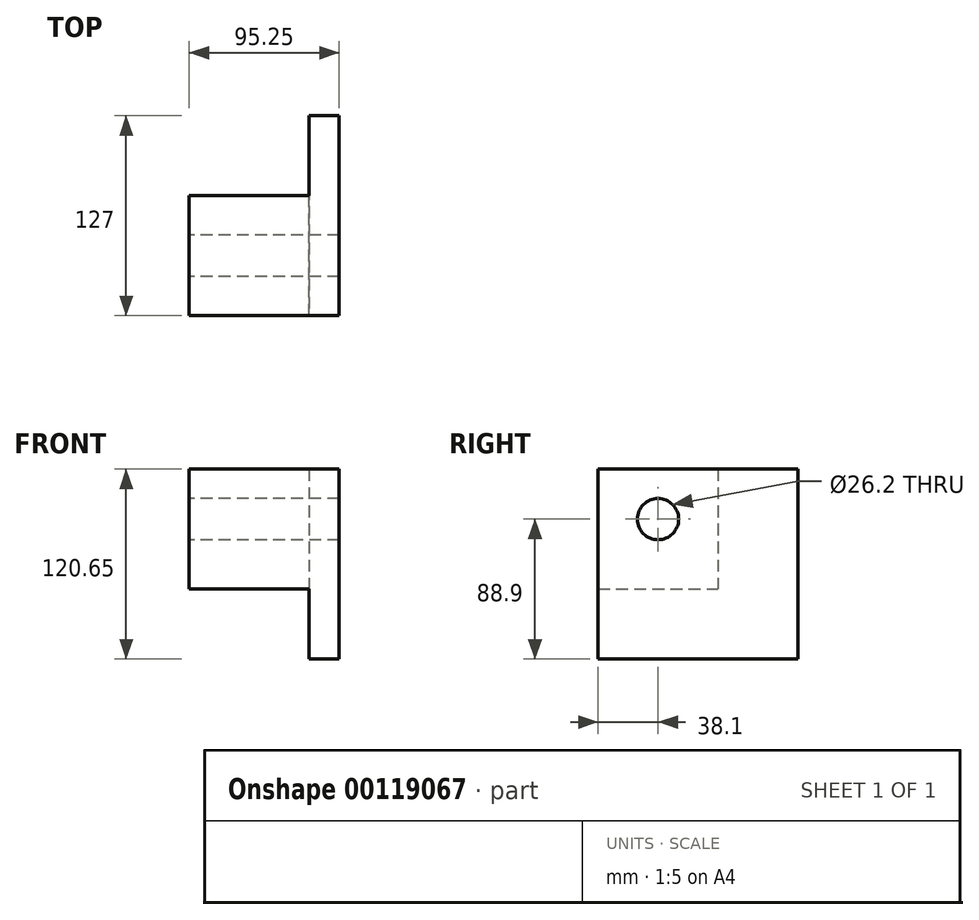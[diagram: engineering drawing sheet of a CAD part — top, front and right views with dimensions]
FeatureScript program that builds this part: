
annotation { "Feature Type Name" : "Feature", "Feature Type Description" : "" }
export const myFeature = defineFeature(function(context is Context, id is Id, definition is map)
    precondition{}
    {
        {
            var Q0;
            Q0=qCreatedBy(makeId("Front.planeOp"),FACE);
            var sketch = newSketch(context, id + "F0", { "sketchPlane" : qUnion([Q0])});
            skArc(sketch, "E0", {"start": v(0, 120.65) * mm, "mid": v(85.31, 85.31) * mm, "end": v(120.65, 0) * mm});
            skLineSegment(sketch, "E1", {"start": v(0, 0) * mm, "end": v(120.65, 0) * mm});
            skLineSegment(sketch, "E2", {"start": v(0, 0) * mm, "end": v(0, 120.65) * mm});
            skLineSegment(sketch, "E3.bottom", {"start": v(0, 120.65) * mm, "end": v(-19.05, 120.65) * mm});
            skLineSegment(sketch, "E3.top", {"start": v(0, 0) * mm, "end": v(-19.05, 0) * mm});
            skLineSegment(sketch, "E3.left", {"start": v(0, 120.65) * mm, "end": v(0, 0) * mm});
            skLineSegment(sketch, "E3.right", {"start": v(-19.05, 120.65) * mm, "end": v(-19.05, 0) * mm});
            skSolve(sketch);
        }
        {
            var Q0;
            Q0=makeQuery(id+"F0.imprint","IMPRINT",FACE,{"disambiguationData":[TD([[makeQuery(id+"F0.imprint","IMPRINT",EDGE,{"derivedFrom":sQuery(id+"F0.wireOp",EDGE,"E0")}),-1.0]])]});
            var Q1;
            Q1=makeQuery(id+"F0.imprint","IMPRINT",FACE,{"disambiguationData":[TD([[makeQuery(id+"F0.imprint","IMPRINT",EDGE,{"derivedFrom":sQuery(id+"F0.wireOp",EDGE,"E3.bottom")}),1.0]])]});
            extrude(context, id + "F1", {"entities" : qUnion([Q0, Q1]), "oppositeDirection" : true, "depth" : 127 * mm});
        }
        {
            var Q0;
            Q0=makeQuery(id+"F1.opExtrude","SWEPT_FACE",FACE,{"disambiguationData":[OSD([sQuery(id+"F0.wireOp",EDGE,"E3.right")])]});
            var sketch = newSketch(context, id + "F2", { "sketchPlane" : qUnion([Q0])});
            skLineSegment(sketch, "E4.bottom", {"start": v(0, 120.65) * mm, "end": v(-76.2, 120.65) * mm});
            skLineSegment(sketch, "E4.top", {"start": v(0, 44.45) * mm, "end": v(-76.2, 44.45) * mm});
            skLineSegment(sketch, "E4.left", {"start": v(0, 120.65) * mm, "end": v(0, 44.45) * mm});
            skLineSegment(sketch, "E4.right", {"start": v(-76.2, 120.65) * mm, "end": v(-76.2, 44.45) * mm});
            skSolve(sketch);
        }
        {
            var Q0;
            Q0=qSketchRegion(id+"F2",true);
            extrude(context, id + "F3", {"entities" : qUnion([Q0]), "operationType" : NewBodyOperationType.ADD, "depth" : 76.2 * mm});
        }
        {
            var Q0;
            Q0=makeQuery(id+"F3.opExtrude","CAP_FACE",FACE,{"disambiguationData":[OSD([sQuery(id+"F2.wireOp",EDGE,"E4.bottom"),sQuery(id+"F2.wireOp",EDGE,"E4.top"),sQuery(id+"F2.wireOp",EDGE,"E4.left"),sQuery(id+"F2.wireOp",EDGE,"E4.right")])],"isStart":false});
            var sketch = newSketch(context, id + "F4", { "sketchPlane" : qUnion([Q0])});
            skLineSegment(sketch, "E5.bottom", {"start": v(0, 120.65) * mm, "end": v(-38.1, 120.65) * mm});
            skLineSegment(sketch, "E5.top", {"start": v(0, 88.9) * mm, "end": v(-38.1, 88.9) * mm});
            skLineSegment(sketch, "E5.left", {"start": v(0, 120.65) * mm, "end": v(0, 88.9) * mm});
            skLineSegment(sketch, "E5.right", {"start": v(-38.1, 120.65) * mm, "end": v(-38.1, 88.9) * mm});
            skCircle(sketch, "E6", {"center": v(-38.1, 88.9) * mm, "radius": 12.7 * mm});
            skSolve(sketch);
        }
        {
            var Q0;
            Q0=sQuery(id+"F4.wireOp",VERTEX,"E5.top.end");
            var Q1;
            Q1=makeQuery(id+"F1.opExtrude","SWEPT_BODY",BODY,{"disambiguationData":[OSD([sQuery(id+"F0.wireOp",EDGE,"E0"),sQuery(id+"F0.wireOp",EDGE,"E1"),sQuery(id+"F0.wireOp",EDGE,"E3.bottom"),sQuery(id+"F0.wireOp",EDGE,"E3.top"),sQuery(id+"F0.wireOp",EDGE,"E3.right")])]});
            hole(context, id + "F5", {"style" : HoleStyle.SIMPLE, "endStyle" : HoleEndStyle.THROUGH, "standardTappedOrClearance" : lookupTablePath({ "standard" : "ANSI", "fit" : "Normal (ASME)", "size" : "1", "type" : "Clearance" }), "standardBlindInLast" : lookupTablePath({ "fit" : "Free", "standard" : "ANSI", "size" : "1", "type" : "Clearance" }), "holeDiameter" : 26.2 * mm, "locations" : qUnion([Q0]), "scope" : qUnion([Q1]), "isTappedThrough" : true});
        }
        {
            var Q0;
            Q0=makeQuery(id+"F3.boolean.opBoolean","MERGE",FACE,{"derivedFrom":[makeQuery(id+"F1.opExtrude","CAP_FACE",FACE,{"disambiguationData":[OSD([sQuery(id+"F0.wireOp",EDGE,"E0"),sQuery(id+"F0.wireOp",EDGE,"E1"),sQuery(id+"F0.wireOp",EDGE,"E3.bottom"),sQuery(id+"F0.wireOp",EDGE,"E3.top"),sQuery(id+"F0.wireOp",EDGE,"E3.right")])],"isStart":true}),makeQuery(id+"F3.opExtrude","SWEPT_FACE",FACE,{"disambiguationData":[OSD([sQuery(id+"F2.wireOp",EDGE,"E4.left")])]})]});
            var sketch = newSketch(context, id + "F6", { "sketchPlane" : qUnion([Q0])});
            skLineSegment(sketch, "E7.bottom", {"start": v(120.65, 0) * mm, "end": v(57.15, 0) * mm});
            skLineSegment(sketch, "E7.top", {"start": v(120.65, 44.45) * mm, "end": v(57.15, 44.45) * mm});
            skLineSegment(sketch, "E7.left", {"start": v(120.65, 0) * mm, "end": v(120.65, 44.45) * mm});
            skLineSegment(sketch, "E7.right", {"start": v(57.15, 0) * mm, "end": v(57.15, 44.45) * mm});
            skCircle(sketch, "E8", {"center": v(57.15, 44.45) * mm, "radius": 12.7 * mm});
            skSolve(sketch);
        }
        {
            var Q0;
            Q0=sQuery(id+"F6.wireOp",VERTEX,"E7.top.end");
            var Q1;
            Q1=makeQuery(id+"F1.opExtrude","SWEPT_BODY",BODY,{"disambiguationData":[OSD([sQuery(id+"F0.wireOp",EDGE,"E0"),sQuery(id+"F0.wireOp",EDGE,"E1"),sQuery(id+"F0.wireOp",EDGE,"E3.bottom"),sQuery(id+"F0.wireOp",EDGE,"E3.top"),sQuery(id+"F0.wireOp",EDGE,"E3.right")])]});
            hole(context, id + "F7", {"style" : HoleStyle.SIMPLE, "endStyle" : HoleEndStyle.THROUGH, "holeDiameter" : 25.4 * mm, "locations" : qUnion([Q0]), "scope" : qUnion([Q1]), "isTappedThrough" : true});
        }
    });
